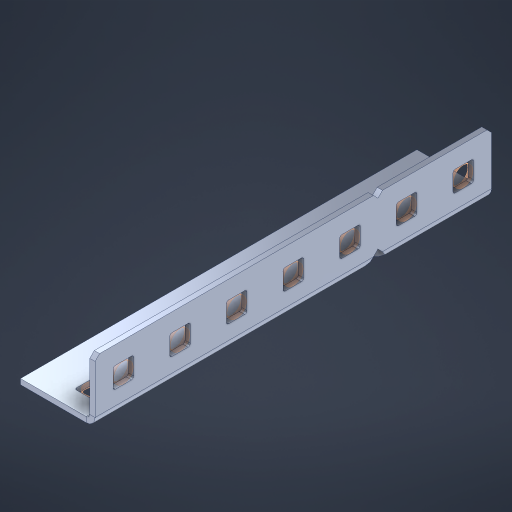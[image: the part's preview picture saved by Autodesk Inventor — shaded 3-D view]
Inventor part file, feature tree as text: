
AUTODESK INVENTOR PART (.ipt)
format: ipt  version: 2023 (Build 270158000, 158)  size: 493,056 bytes
history: native  units: in
note: dims shown in document units (in); Inventor stores cm internally (conversion verified against a paired STEP export)
features: other x19, extrude x13, sheet_metal_op x10, sketch x8, mirror x1, pattern_linear x1, chamfer x1
ambient origin geometry x8: Origin, YZ Plane, XZ Plane, XY Plane, X Axis, Y Axis, Z Axis, Center Point
bodies: Solid1 (feature_tree), Body (feature_tree)
feature tree (53):
  other  "Flange Pattern Plane"
  sheet_metal_op  "Flange Pattern"
  sheet_metal_op  "Body Pattern"
  other  "Arc Length"
  mirror  "Notch Mirror"
  pattern_linear  "Notch Pattern"  Spacing1=0.1875in  [1 undecoded]
  chamfer  "End Chamfer"
  extrude  "Half Cut"  Depth=0.0469in
  sketch  "Sketch1"  dims[d0=2.5in]
  other  "Plate1"
  sketch  "Sketch2"  dims[d1=3.5in]
  other  "Plate2"
  sheet_metal_op  "Bend1"
  sheet_metal_op  "Corner1"
  sketch  "Sketch3"  dims[d2=0.0469in]
  other  "Flange Pattern Sketch"
  sketch  "Sketch7"  dims[d3=0.0469in]
  other  "Srf1"
  other  "Srf2"
  sketch  "Sketch8"  dims[d4=0.0234in]
  sketch  "Sketch9"  dims[d5=0.0938in]
  other  "Srf91"
  sheet_metal_op  "Body Pattern Sketch"
  other  "Srf92"
  sketch  "Sketch13"  dims[d6=0.0469in]
  sketch  "Sketch14"  dims[d7=0.5in d8=90.0deg d9=0.0312in d10=0.1875in d11=0.0469in d12=0.0469in d16=0.182in d17=0.02in d18=0.0469in d19=0.0in d20=0.25in d21=0.25in d46=0.172in d47=1.0in d48=0.0in d49=0.182in d50=0.02in d51=0.25in d52=0.25in d53=0.0469in d54=0.0in d55=0.172in d56=1.0in d57=0.0in d60=2.7559in d62=0.5in d63=0.3937in d65=0.5in d85=0.1227in d86=0.1659in d88=0.04in d89=0.0469in d90=0.0in d91=0.04in d92=0.0491in d95=2.5in d96=0.04in d97=0.25in d98=45.0deg d101=0.0in d102=2.497in d131=0.5in d132=2.7559in d134=0.5in d139=0.5in]
  other  "Srf856"
  other  "Srf1310"
  other  "Srf1311"
  other  "Srf1312"
  other  "Srf1376"
  other  "Srf1377"
  other  "Srf1728"
  other  "Srf1755"
  other  "Srf1878"
  other  "Srf1942"
  sheet_metal_op  "Flange Stamp"
  sheet_metal_op  "Flange Circle"
  sheet_metal_op  "Body Stamp"
  sheet_metal_op  "Body Circle"
  sheet_metal_op  "Notch"
  extrude  "ExtrusionSrf2"  Depth=0.0469in
  extrude  "ExtrusionSrf92"  Depth=0.5in
  extrude  "ExtrusionSrf856"  Depth=0.02in
  extrude  "ExtrusionSrf1310"  Depth=0.0469in
  extrude  "ExtrusionSrf1311"  TaperAngle=0.0deg  [1 undecoded]
  extrude  "ExtrusionSrf1312"  Depth=0.5in
  extrude  "ExtrusionSrf1376"  Depth=0.5in
  extrude  "ExtrusionSrf1377"  Depth=0.5in
  extrude  "ExtrusionSrf1728"  Depth=0.5in TaperAngle=0.0deg
  extrude  "ExtrusionSrf1755"  Depth=0.5in
  extrude  "ExtrusionSrf1878"  Depth=0.02in
  extrude  "ExtrusionSrf1942"  Depth=0.5in
note: 2 required parameter values undecoded (feature->parameter linkage not recoverable at this tier; creation-order binding heuristic only, values carry confidence <= 0.55)
